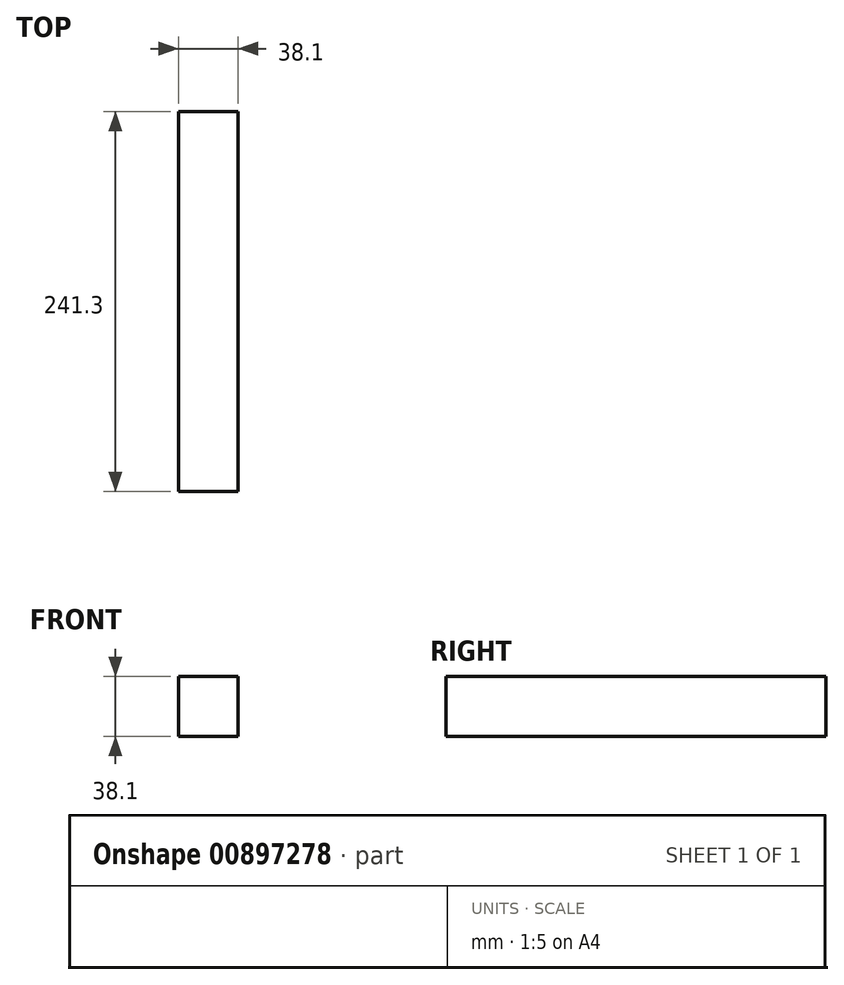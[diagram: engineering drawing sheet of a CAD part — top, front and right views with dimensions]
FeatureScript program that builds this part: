
annotation { "Feature Type Name" : "Feature", "Feature Type Description" : "" }
export const myFeature = defineFeature(function(context is Context, id is Id, definition is map)
    precondition{}
    {
        {
            var Q0;
            Q0=qCreatedBy(makeId("Front.planeOp"),FACE);
            var sketch = newSketch(context, id + "F0", { "sketchPlane" : qUnion([Q0])});
            skLineSegment(sketch, "E0.bottom", {"start": v(-19.05, 19.05) * mm, "end": v(19.05, 19.05) * mm});
            skLineSegment(sketch, "E0.top", {"start": v(-19.05, -19.05) * mm, "end": v(19.05, -19.05) * mm});
            skLineSegment(sketch, "E0.left", {"start": v(-19.05, 19.05) * mm, "end": v(-19.05, -19.05) * mm});
            skLineSegment(sketch, "E0.right", {"start": v(19.05, 19.05) * mm, "end": v(19.05, -19.05) * mm});
            skPoint(sketch, "E0.middle", {"position": v(0, 0) * mm});
            skSolve(sketch);
        }
        {
            var Q0;
            Q0=makeQuery(id+"F0.imprint","IMPRINT",FACE,{"disambiguationData":[TD([[makeQuery(id+"F0.imprint","IMPRINT",EDGE,{"derivedFrom":sQuery(id+"F0.wireOp",EDGE,"E0.bottom")}),-1.0]])]});
            extrude(context, id + "F1", {"entities" : qUnion([Q0]), "depth" : 241.3 * mm, "offsetDistance" : 25.4 * mm});
        }
    });
